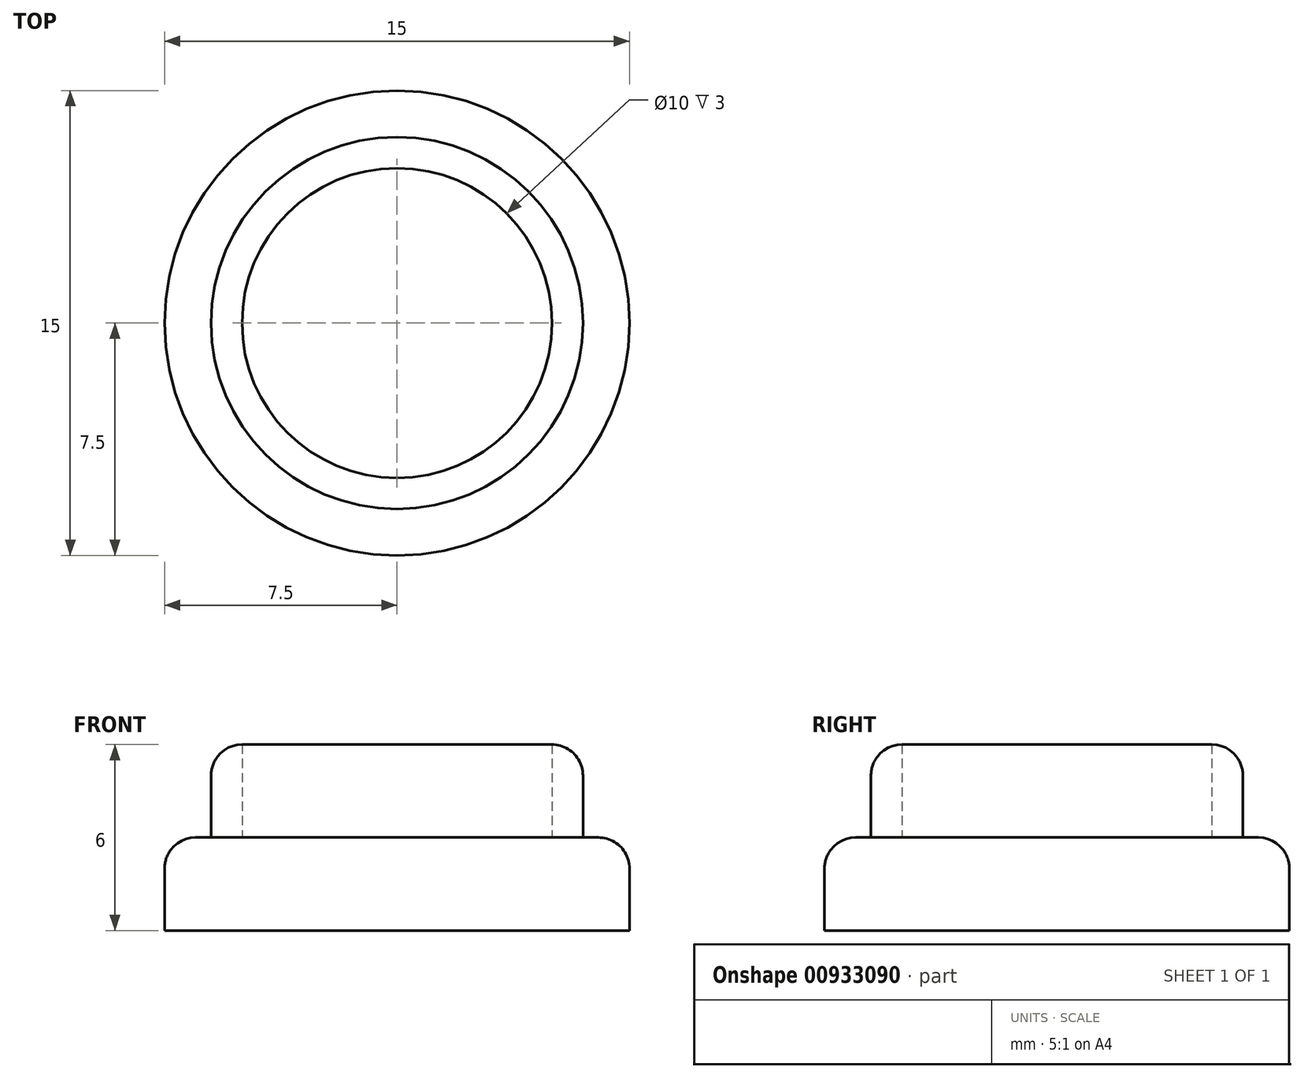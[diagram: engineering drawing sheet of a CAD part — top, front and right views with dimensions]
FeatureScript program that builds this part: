
annotation { "Feature Type Name" : "Feature", "Feature Type Description" : "" }
export const myFeature = defineFeature(function(context is Context, id is Id, definition is map)
    precondition{}
    {
        {
            var Q0;
            Q0=qCreatedBy(makeId("Top.planeOp"),FACE);
            var sketch = newSketch(context, id + "F0", { "sketchPlane" : qUnion([Q0])});
            skCircle(sketch, "E0", {"center": v(0, 0) * mm, "radius": 7.5 * mm});
            skCircle(sketch, "E1", {"center": v(0, 0) * mm, "radius": 5 * mm});
            skCircle(sketch, "E2", {"center": v(0, 0) * mm, "radius": 6 * mm});
            skSolve(sketch);
        }
        {
            var Q0;
            Q0=makeQuery(id+"F0.imprint","IMPRINT",FACE,{"disambiguationData":[TD([[makeQuery(id+"F0.imprint","IMPRINT",EDGE,{"derivedFrom":sQuery(id+"F0.wireOp",EDGE,"E0")}),1.0]])]});
            var Q1;
            Q1=makeQuery(id+"F0.imprint","IMPRINT",FACE,{"disambiguationData":[TD([[makeQuery(id+"F0.imprint","IMPRINT",EDGE,{"derivedFrom":sQuery(id+"F0.wireOp",EDGE,"E1")}),1.0]])]});
            var Q2;
            Q2=makeQuery(id+"F0.imprint","IMPRINT",FACE,{"disambiguationData":[TD([[makeQuery(id+"F0.imprint","IMPRINT",EDGE,{"derivedFrom":sQuery(id+"F0.wireOp",EDGE,"E1")}),-1.0]])]});
            extrude(context, id + "F1", {"entities" : qUnion([Q0, Q1, Q2]), "depth" : -3 * mm, "offsetDistance" : 25 * mm});
        }
        {
            var Q0;
            Q0=makeQuery(id+"F0.imprint","IMPRINT",FACE,{"disambiguationData":[TD([[makeQuery(id+"F0.imprint","IMPRINT",EDGE,{"derivedFrom":sQuery(id+"F0.wireOp",EDGE,"E1")}),-1.0]])]});
            extrude(context, id + "F2", {"entities" : qUnion([Q0]), "operationType" : NewBodyOperationType.ADD, "depth" : 3 * mm, "offsetDistance" : 25 * mm});
        }
        {
            var Q0;
            Q0=makeQuery(id+"F1.opExtrude","CAP_EDGE",EDGE,{"disambiguationData":[OSD([sQuery(id+"F0.wireOp",EDGE,"E0")])],"isStart":true});
            var Q1;
            Q1=makeQuery(id+"F2.opExtrude","CAP_EDGE",EDGE,{"disambiguationData":[OSD([sQuery(id+"F0.wireOp",EDGE,"E2")])],"isStart":false});
            fillet(context, id + "F3", {"entities" : qUnion([Q0, Q1]), "radius" : 1 * mm, "tangentPropagation" : true, "allowEdgeOverflow" : false});
        }
    });
